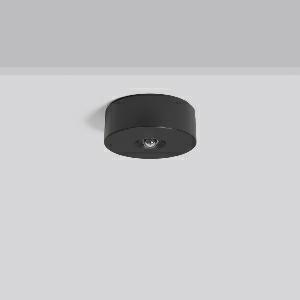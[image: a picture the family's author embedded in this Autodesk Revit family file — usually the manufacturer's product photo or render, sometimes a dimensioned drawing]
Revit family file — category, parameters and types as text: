
# Revit family: lucio_2_672527_003_04_53dd
name_source: partatom
category: Lighting Fixtures
units: mm (PartAtom-declared; Revit-internal decimal feet)

## family parameters
Cut with Voids When Loaded = No
Host = Face
Light Source = No
Part Type = Normal
Room Calculation Point = No
Round Connector Dimension = Use Diameter
Shared = No

## types (1)
- Linse asymmetrisch 3h (1 x LED Modul 740, 230 lm, 4000)
    Apparent Load = 0 VA
    CIE Flux Codes = 64 84 96 100 100
    Color Rendering = 70
    Color Temperature = 4000
    Default Elevation = 1800 mm
    Description = Series: LUCIO 2
Round surface-mounted downlight. For escape route illumination. Housing: plastic (polycarbonate). Cover: polycarbonate. Plastic lenses for area lighting and escape route illumination included in scope of delivery. Suitable for Ceiling mounting. Self-contained system with automatic self-test and feedback to the RZB monitoring system MULTIDIGIT. 
Colour: black
Diameter: 110 mm
Height: 46 mm
Weight: 0.29 kg
Operating mode: non-maintained power mode
Duration time: 3 h, 8 h
Lamp: LED
Socket: without socket
Colour temperature: 4000K
Colour rendering index (CRI): 70
Luminous flux, emergency: 240 lm
System power, emergency: -
Luminous flux, emergency 2: 220 lm
System power, emergency 2: -
Luminous flux, emergency 3: 120 lm
System power, emergency 3: -
Luminous flux, emergency 4: 110 lm
Control gear: EB in emergency mode only
Protection class: II
Type of protection: IP 20
    Height = 46 mm
    Lamp = 1 x LED Modul 740
    Lamp Light Flux = 230 lm
    Lamp count = 1
    Length = 110 mm
    Lifetime = 50000 h
    Luminous efficacy = 0 lm/W
    Manufacturer = RZB
    ModVariant = No
    Model = 672527.003.04
    Mounting Place = Ceiling
    Mounting Type = Surface mounted
    Number of Poles = 1
    OnlyDefault = Yes
    Power Factor = 1
    Product Name = LUCIO 2
    Product group = Surface mounted ceiling luminaires
    ProductGroupID = 303
    Protection Class = Protection class II
    Protection Degree = Degree of protection
    RLX_Detail_Level = 1
    RLX_Emergency_Light_Flux = 240 lm
    RLX_Emergency_Type = 3
    RLX_Emergency_Type_DB = Yes
    RlxData = <blob elided: 200809 chars, md5=18355abb>
    Socket = socket
    Standby Power = 0 W
    System Light Flux = 0 lm
    System Power = 0 W
    Type Comments = Lens asymmetric 3h
    Type Image = 672527.003.jpg
    URL = http://relux.com
    VarID = linse_asymmetrisch_3h
    Voltage = 0 V
    Weight = 0.00 kg
    Width = 0 mm  [stored 0 ft]

note: [stored X ft] marks values corroborated as IEEE doubles in the binary element streams (Revit-internal decimal feet)

## geometry (parser evidence)
native form markers: Blend x4, Sweep x13
no freeform markers — native parametric forms only
